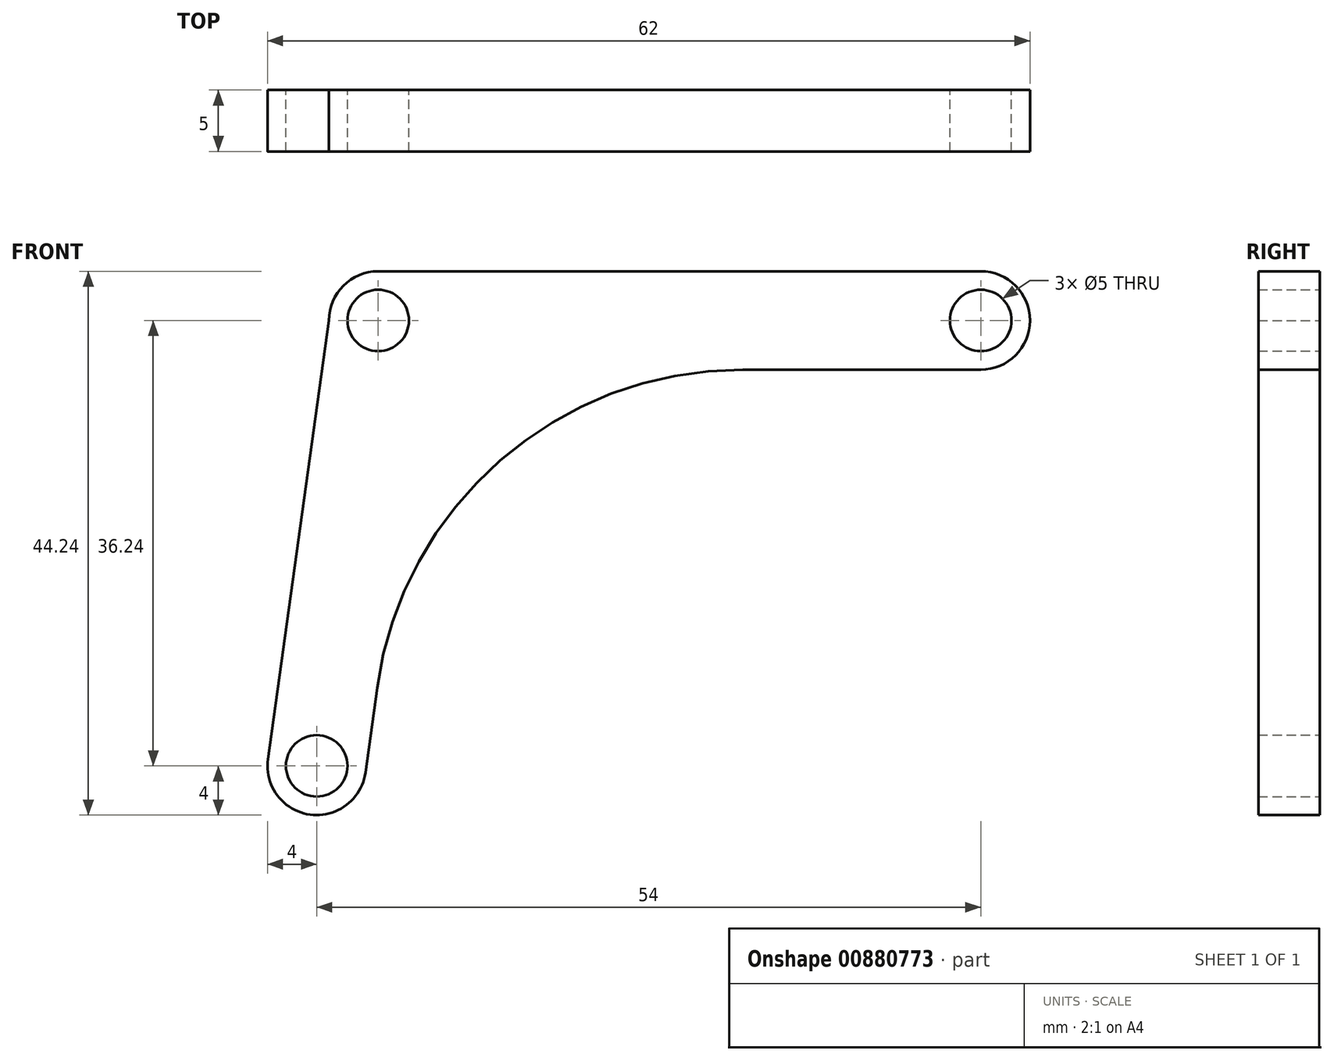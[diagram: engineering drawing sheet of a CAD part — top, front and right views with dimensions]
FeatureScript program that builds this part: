
annotation { "Feature Type Name" : "Feature", "Feature Type Description" : "" }
export const myFeature = defineFeature(function(context is Context, id is Id, definition is map)
    precondition{}
    {
        {
            var Q0;
            Q0=qCreatedBy(makeId("Front.planeOp"),FACE);
            var sketch = newSketch(context, id + "F0", { "sketchPlane" : qUnion([Q0])});
            skCircle(sketch, "E0", {"center": v(0, 0) * mm, "radius": 2.5 * mm});
            skArc(sketch, "E1", {"start": v(0, 4) * mm, "mid": v(-2.83, 2.83) * mm, "end": v(-4, 0) * mm});
            skCircle(sketch, "E2", {"center": v(49, 0) * mm, "radius": 2.5 * mm});
            skArc(sketch, "E3", {"start": v(49, -4) * mm, "mid": v(53, 0) * mm, "end": v(49, 4) * mm});
            skCircle(sketch, "E4", {"center": v(-5, -36.24) * mm, "radius": 2.5 * mm});
            skArc(sketch, "E5", {"start": v(-8.96, -35.69) * mm, "mid": v(-5.55, -40.2) * mm, "end": v(-1.04, -36.79) * mm});
            skLineSegment(sketch, "E6", {"start": v(0, 4) * mm, "end": v(49, 4) * mm});
            skLineSegment(sketch, "E7", {"start": v(3.49, -4) * mm, "end": v(49, -4) * mm});
            skLineSegment(sketch, "E8", {"start": v(-4, 0) * mm, "end": v(-8.96, -35.69) * mm});
            skLineSegment(sketch, "E9", {"start": v(3.49, -4) * mm, "end": v(-1.04, -36.79) * mm});
            skArc(sketch, "E10", {"start": v(29.63, -4) * mm, "mid": v(9.92, -11.38) * mm, "end": v(-0.09, -29.9) * mm});
            skSolve(sketch);
        }
        {
            var Q0;
            Q0 = qSketchRegion(id + "F0", true);
            extrude(context, id + "F1", {"entities" : qUnion([Q0]), "depth" : 5 * mm, "offsetDistance" : 25 * mm});
        }
    });
